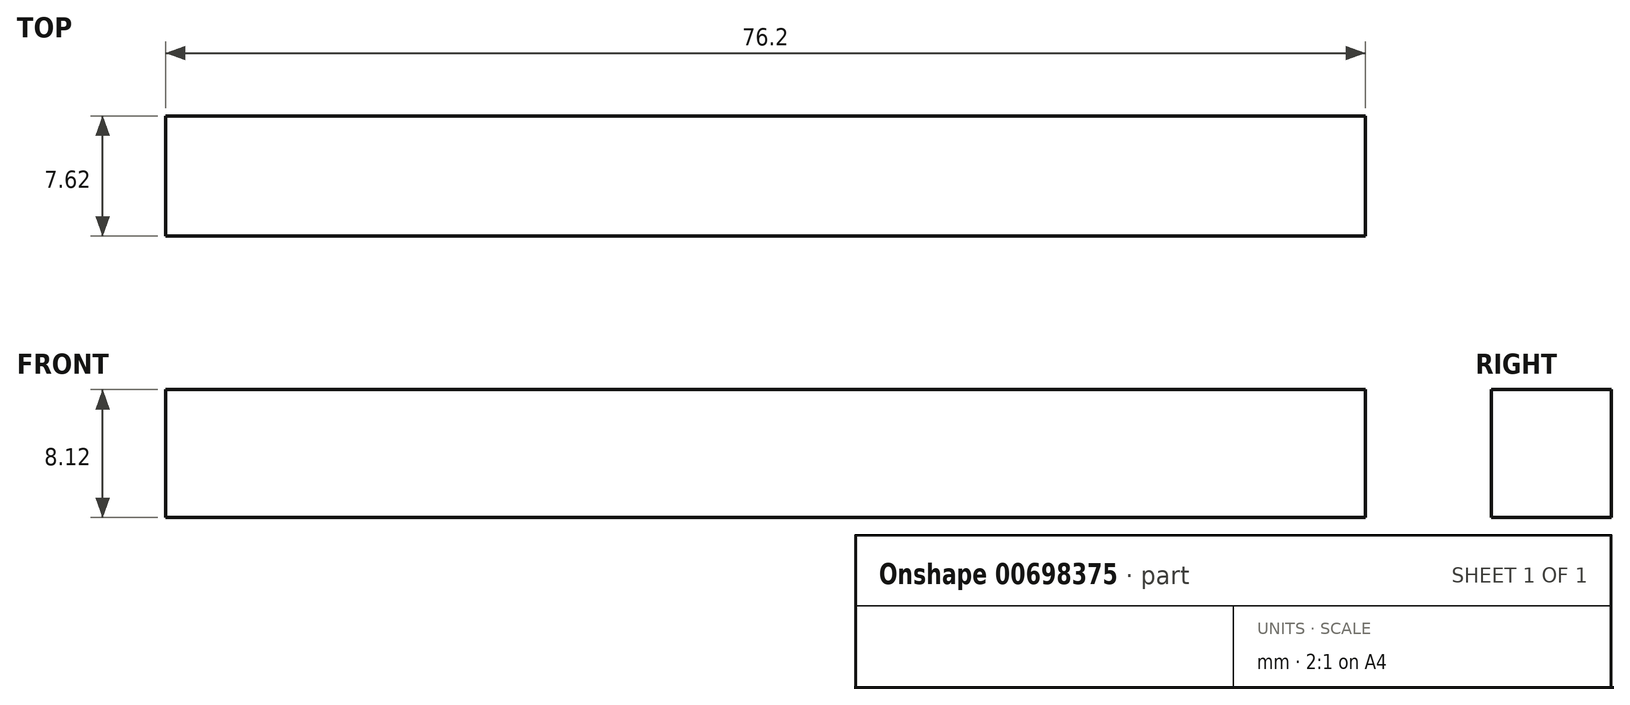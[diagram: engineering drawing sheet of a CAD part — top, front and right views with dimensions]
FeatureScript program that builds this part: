
annotation { "Feature Type Name" : "Feature", "Feature Type Description" : "" }
export const myFeature = defineFeature(function(context is Context, id is Id, definition is map)
    precondition{}
    {
        {
            var Q0;
            Q0=qCreatedBy(makeId("Front.planeOp"),FACE);
            var sketch = newSketch(context, id + "F0", { "sketchPlane" : qUnion([Q0])});
            skLineSegment(sketch, "E0.bottom", {"start": v(-42.52, -16.37) * mm, "end": v(33.68, -16.37) * mm});
            skLineSegment(sketch, "E0.top", {"start": v(-42.52, -8.25) * mm, "end": v(33.68, -8.25) * mm});
            skLineSegment(sketch, "E0.left", {"start": v(-42.52, -16.37) * mm, "end": v(-42.52, -8.25) * mm});
            skLineSegment(sketch, "E0.right", {"start": v(33.68, -16.37) * mm, "end": v(33.68, -8.25) * mm});
            skSolve(sketch);
        }
        {
            var Q0;
            Q0=makeQuery(id+"F0.imprint","IMPRINT",FACE,{"disambiguationData":[TD([[makeQuery(id+"F0.imprint","IMPRINT",EDGE,{"derivedFrom":sQuery(id+"F0.wireOp",EDGE,"E0.bottom")}),1.0]])]});
            extrude(context, id + "F1", {"entities" : qUnion([Q0]), "depth" : 7.62 * mm, "offsetDistance" : 25.4 * mm});
        }
    });
